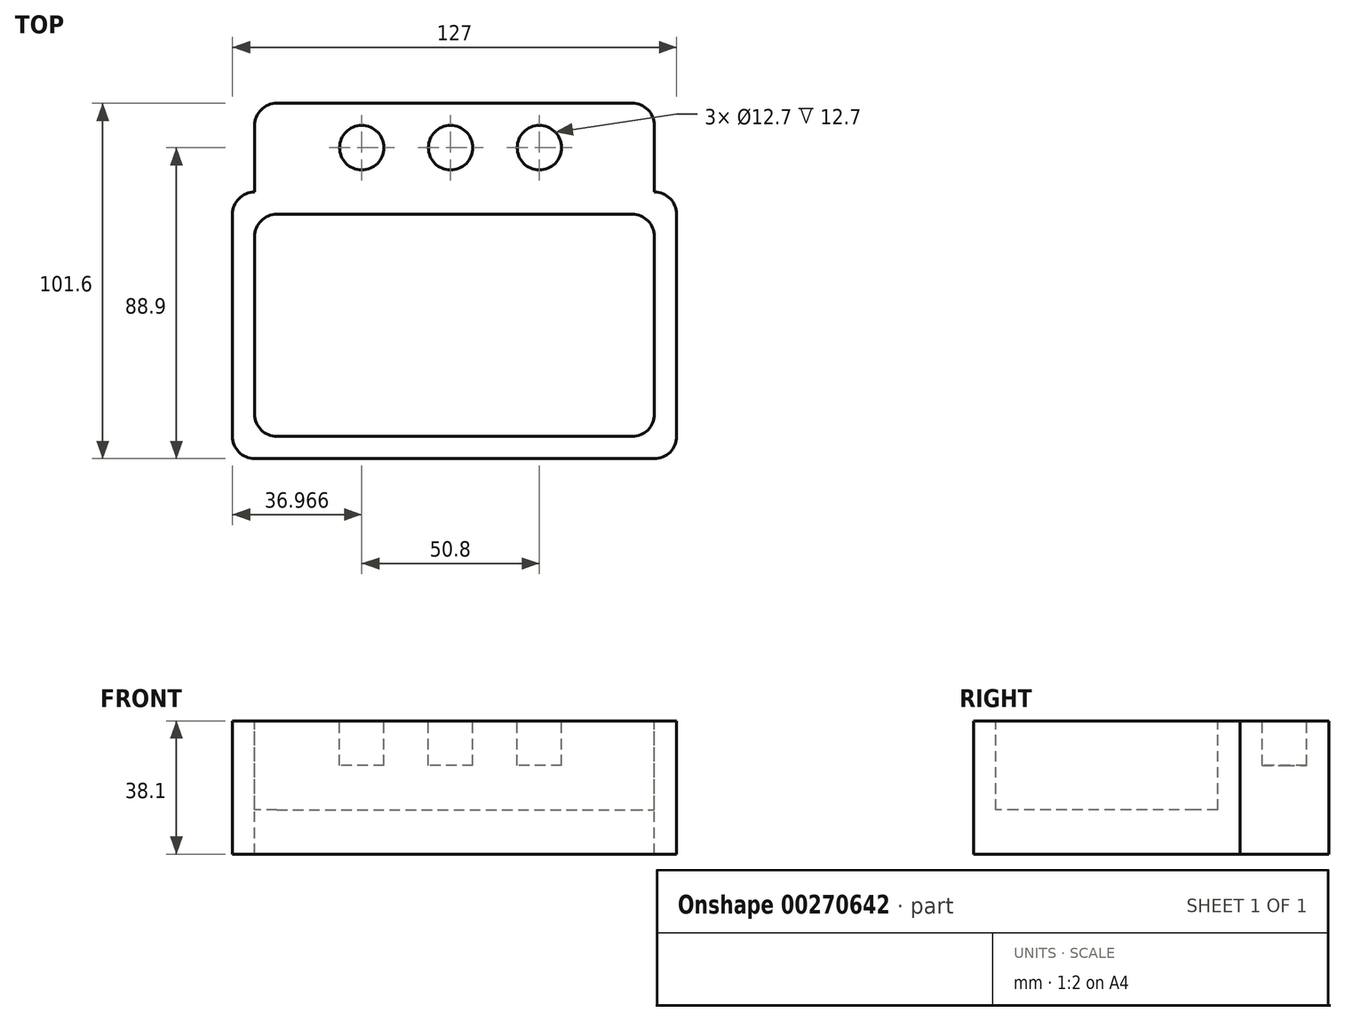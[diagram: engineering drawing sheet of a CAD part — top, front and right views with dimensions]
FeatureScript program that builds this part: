
annotation { "Feature Type Name" : "Feature", "Feature Type Description" : "" }
export const myFeature = defineFeature(function(context is Context, id is Id, definition is map)
    precondition{}
    {
        {
            var Q0;
            Q0=qCreatedBy(makeId("Top.planeOp"),FACE);
            var sketch = newSketch(context, id + "F0", { "sketchPlane" : qUnion([Q0])});
            skLineSegment(sketch, "E0.bottom", {"start": v(-57.15, -38.1) * mm, "end": v(57.15, -38.1) * mm});
            skLineSegment(sketch, "E0.top", {"start": v(-57.15, 38.1) * mm, "end": v(57.15, 38.1) * mm});
            skLineSegment(sketch, "E0.left", {"start": v(-63.5, -31.75) * mm, "end": v(-63.5, 31.75) * mm});
            skLineSegment(sketch, "E0.right", {"start": v(63.5, -31.75) * mm, "end": v(63.5, 31.75) * mm});
            skPoint(sketch, "E0.middle", {"position": v(0, 0) * mm});
            skLineSegment(sketch, "E1.bottom", {"start": v(-50.8, 31.75) * mm, "end": v(50.8, 31.75) * mm});
            skLineSegment(sketch, "E1.top", {"start": v(-50.8, -31.75) * mm, "end": v(50.8, -31.75) * mm});
            skLineSegment(sketch, "E1.left", {"start": v(-57.15, 25.4) * mm, "end": v(-57.15, -25.4) * mm});
            skLineSegment(sketch, "E1.right", {"start": v(57.15, 25.4) * mm, "end": v(57.15, -25.4) * mm});
            skPoint(sketch, "E2.visualSharp", {"position": v(-57.15, 31.75) * mm});
            skArc(sketch, "E2.filletArc", {"start": v(-50.8, 31.75) * mm, "mid": v(-55.3, 29.9) * mm, "end": v(-57.15, 25.4) * mm});
            skPoint(sketch, "E3.visualSharp", {"position": v(-63.5, 38.1) * mm});
            skArc(sketch, "E3.filletArc", {"start": v(-57.15, 38.1) * mm, "mid": v(-61.64, 36.24) * mm, "end": v(-63.5, 31.75) * mm});
            skPoint(sketch, "E4.visualSharp", {"position": v(-57.15, -31.75) * mm});
            skArc(sketch, "E4.filletArc", {"start": v(-57.15, -25.4) * mm, "mid": v(-55.3, -29.9) * mm, "end": v(-50.8, -31.75) * mm});
            skPoint(sketch, "E5.visualSharp", {"position": v(-63.5, -38.1) * mm});
            skArc(sketch, "E5.filletArc", {"start": v(-63.5, -31.75) * mm, "mid": v(-61.64, -36.24) * mm, "end": v(-57.15, -38.1) * mm});
            skPoint(sketch, "E6.visualSharp", {"position": v(57.15, 31.75) * mm});
            skArc(sketch, "E6.filletArc", {"start": v(57.15, 25.4) * mm, "mid": v(55.3, 29.9) * mm, "end": v(50.8, 31.75) * mm});
            skPoint(sketch, "E7.visualSharp", {"position": v(63.5, 38.1) * mm});
            skArc(sketch, "E7.filletArc", {"start": v(63.5, 31.75) * mm, "mid": v(61.64, 36.24) * mm, "end": v(57.15, 38.1) * mm});
            skPoint(sketch, "E8.visualSharp", {"position": v(57.15, -31.75) * mm});
            skArc(sketch, "E8.filletArc", {"start": v(50.8, -31.75) * mm, "mid": v(55.3, -29.9) * mm, "end": v(57.15, -25.4) * mm});
            skPoint(sketch, "E9.visualSharp", {"position": v(63.5, -38.1) * mm});
            skArc(sketch, "E9.filletArc", {"start": v(57.15, -38.1) * mm, "mid": v(61.64, -36.24) * mm, "end": v(63.5, -31.75) * mm});
            skLineSegment(sketch, "E10.top", {"start": v(-50.8, 63.5) * mm, "end": v(50.8, 63.5) * mm});
            skLineSegment(sketch, "E10.left", {"start": v(-57.15, 38.1) * mm, "end": v(-57.15, 57.15) * mm});
            skLineSegment(sketch, "E10.right", {"start": v(57.15, 38.1) * mm, "end": v(57.15, 57.15) * mm});
            skPoint(sketch, "E11.visualSharp", {"position": v(-57.15, 63.5) * mm});
            skArc(sketch, "E11.filletArc", {"start": v(-50.8, 63.5) * mm, "mid": v(-55.3, 61.64) * mm, "end": v(-57.15, 57.15) * mm});
            skPoint(sketch, "E12.visualSharp", {"position": v(57.15, 63.5) * mm});
            skArc(sketch, "E12.filletArc", {"start": v(57.15, 57.15) * mm, "mid": v(55.3, 61.64) * mm, "end": v(50.8, 63.5) * mm});
            skCircle(sketch, "E13", {"center": v(-1.13, 50.8) * mm, "radius": 6.35 * mm});
            skCircle(sketch, "E14", {"center": v(-26.53, 50.8) * mm, "radius": 6.35 * mm});
            skCircle(sketch, "E15", {"center": v(24.27, 50.8) * mm, "radius": 6.35 * mm});
            skSolve(sketch);
        }
        {
            var Q0;
            Q0=makeQuery(id+"F0.imprint","IMPRINT",FACE,{"disambiguationData":[TD([[makeQuery(id+"F0.imprint","IMPRINT",EDGE,{"derivedFrom":sQuery(id+"F0.wireOp",EDGE,"E1.bottom")}),-1.0]])]});
            var Q1;
            Q1=makeQuery(id+"F0.imprint","IMPRINT",FACE,{"disambiguationData":[TD([[makeQuery(id+"F0.imprint","IMPRINT",EDGE,{"derivedFrom":sQuery(id+"F0.wireOp",EDGE,"E0.bottom")}),1.0]])]});
            var Q2;
            Q2=makeQuery(id+"F0.imprint","IMPRINT",FACE,{"disambiguationData":[TD([[makeQuery(id+"F0.imprint","IMPRINT",EDGE,{"derivedFrom":sQuery(id+"F0.wireOp",EDGE,"E0.top")}),1.0]])]});
            var Q3;
            Q3=makeQuery(id+"F0.imprint","IMPRINT",FACE,{"disambiguationData":[TD([[makeQuery(id+"F0.imprint","IMPRINT",EDGE,{"derivedFrom":sQuery(id+"F0.wireOp",EDGE,"E14")}),1.0]])]});
            var Q4;
            Q4=makeQuery(id+"F0.imprint","IMPRINT",FACE,{"disambiguationData":[TD([[makeQuery(id+"F0.imprint","IMPRINT",EDGE,{"derivedFrom":sQuery(id+"F0.wireOp",EDGE,"E13")}),1.0]])]});
            var Q5;
            Q5=makeQuery(id+"F0.imprint","IMPRINT",FACE,{"disambiguationData":[TD([[makeQuery(id+"F0.imprint","IMPRINT",EDGE,{"derivedFrom":sQuery(id+"F0.wireOp",EDGE,"E15")}),1.0]])]});
            extrude(context, id + "F1", {"entities" : qUnion([Q0, Q1, Q2, Q3, Q4, Q5]), "oppositeDirection" : true, "depth" : 38.1 * mm});
        }
        {
            var Q0;
            Q0=makeQuery(id+"F0.imprint","IMPRINT",FACE,{"disambiguationData":[TD([[makeQuery(id+"F0.imprint","IMPRINT",EDGE,{"derivedFrom":sQuery(id+"F0.wireOp",EDGE,"E1.bottom")}),-1.0]])]});
            extrude(context, id + "F2", {"entities" : qUnion([Q0]), "operationType" : NewBodyOperationType.REMOVE, "oppositeDirection" : true, "depth" : 25.4 * mm});
        }
        {
            var Q0;
            Q0=makeQuery(id+"F0.imprint","IMPRINT",FACE,{"disambiguationData":[TD([[makeQuery(id+"F0.imprint","IMPRINT",EDGE,{"derivedFrom":sQuery(id+"F0.wireOp",EDGE,"E14")}),1.0]])]});
            var Q1;
            Q1=makeQuery(id+"F0.imprint","IMPRINT",FACE,{"disambiguationData":[TD([[makeQuery(id+"F0.imprint","IMPRINT",EDGE,{"derivedFrom":sQuery(id+"F0.wireOp",EDGE,"E13")}),1.0]])]});
            var Q2;
            Q2=makeQuery(id+"F0.imprint","IMPRINT",FACE,{"disambiguationData":[TD([[makeQuery(id+"F0.imprint","IMPRINT",EDGE,{"derivedFrom":sQuery(id+"F0.wireOp",EDGE,"E15")}),1.0]])]});
            extrude(context, id + "F3", {"entities" : qUnion([Q0, Q1, Q2]), "operationType" : NewBodyOperationType.REMOVE, "oppositeDirection" : true, "depth" : 12.7 * mm});
        }
    });
